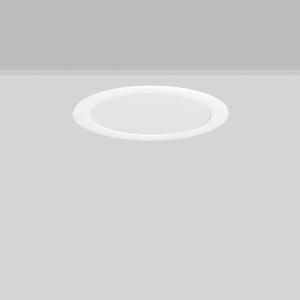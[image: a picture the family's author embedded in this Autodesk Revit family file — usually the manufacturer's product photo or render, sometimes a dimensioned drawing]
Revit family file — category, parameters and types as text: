
# Revit family: toledo_flat_round_e_672231_002_df8e
name_source: partatom
category: Lighting Fixtures
units: mm (PartAtom-declared; Revit-internal decimal feet)

## family parameters
Cut with Voids When Loaded = No
Host = Face
Light Source = No
Part Type = Normal
Room Calculation Point = No
Round Connector Dimension = Use Diameter
Shared = No

## types (1)
- TOLEDO FLAT round E (1 x LED Modul 830, 2150 lm, 3000)
    Apparent Load = 22 VA
    CIE Flux Codes = 49 80 96 100 100
    Color Rendering = 80
    Color Temperature = 3000
    Default Elevation = 1800 mm
    Description = Series: TOLEDO FLAT round
Ultra thin recessed downlight. For escape route illumination. Housing: die-cast aluminium, powder-coated. Lightguide and diffuser made of non-yellowing plastic (PMMA). Diffuser opal matt plastic. Ceiling installation with spring system. Including separate LED converter with connecting cable 250 mm. Suitable for connection to central battery systems. External driver with simple plug-in locking system. 
Colour: white
Diameter: 317 mm
Height: 3 mm
Cut-out diameter: 288 mm
Recess height: 35 mm
Luminaire: recess height: 31-51 mm
Weight: 1.27 kg
Operating mode: maintained power mode
Lamp: LED
Socket: without socket
Colour temperature: 3000K
Colour rendering index (CRI): 80
System power: 22 W
Rated luminous flux: 2150 lm
Luminous flux, emergency: 2150 lm
System power, emergency: 22 W
Control gear: Regulated power supply
Protection class: II
Type of protection: IP 54
    Height = 0 mm  [stored 0 ft]
    Lamp = 1 x LED Modul 830
    Lamp Light Flux = 2150 lm
    Lamp count = 1
    Length = 317 mm
    Lifetime = 50000 h
    Luminous efficacy = 98 lm/W
    Manufacturer = RZB
    ModVariant = No
    Model = 672231.002
    Mounting Place = Ceiling
    Mounting Type = Recessed
    Number of Poles = 1
    OnlyDefault = Yes
    Power Factor = 1
    Product Name = TOLEDO FLAT round E
    Product group = Recessed downlights
    ProductGroupID = 402
    Protection Class = Protection class II
    Protection Degree = IP 40
    RLX_Detail_Level = 1
    RLX_Emergency_Light_Flux = 2150 lm
    RLX_Emergency_Type = 3
    RLX_Emergency_Type_DB = Yes
    RlxData = <blob elided: 30697 chars, md5=62dff47f>
    Socket = socket
    Standby Power = 0 W
    System Light Flux = 2150 lm
    System Power = 22 W
    Type Comments = Product without accessories
    Type Image = 901484.002.jpg
    URL = http://relux.com
    VarID = ---
    Voltage = 230 V
    Voltage Range = 220-240 V
    Weight = 0.00 kg
    Width = 0 mm  [stored 0 ft]

note: [stored X ft] marks values corroborated as IEEE doubles in the binary element streams (Revit-internal decimal feet)

## geometry (parser evidence)
native form markers: Blend x4, Sweep x10
no freeform markers — native parametric forms only
